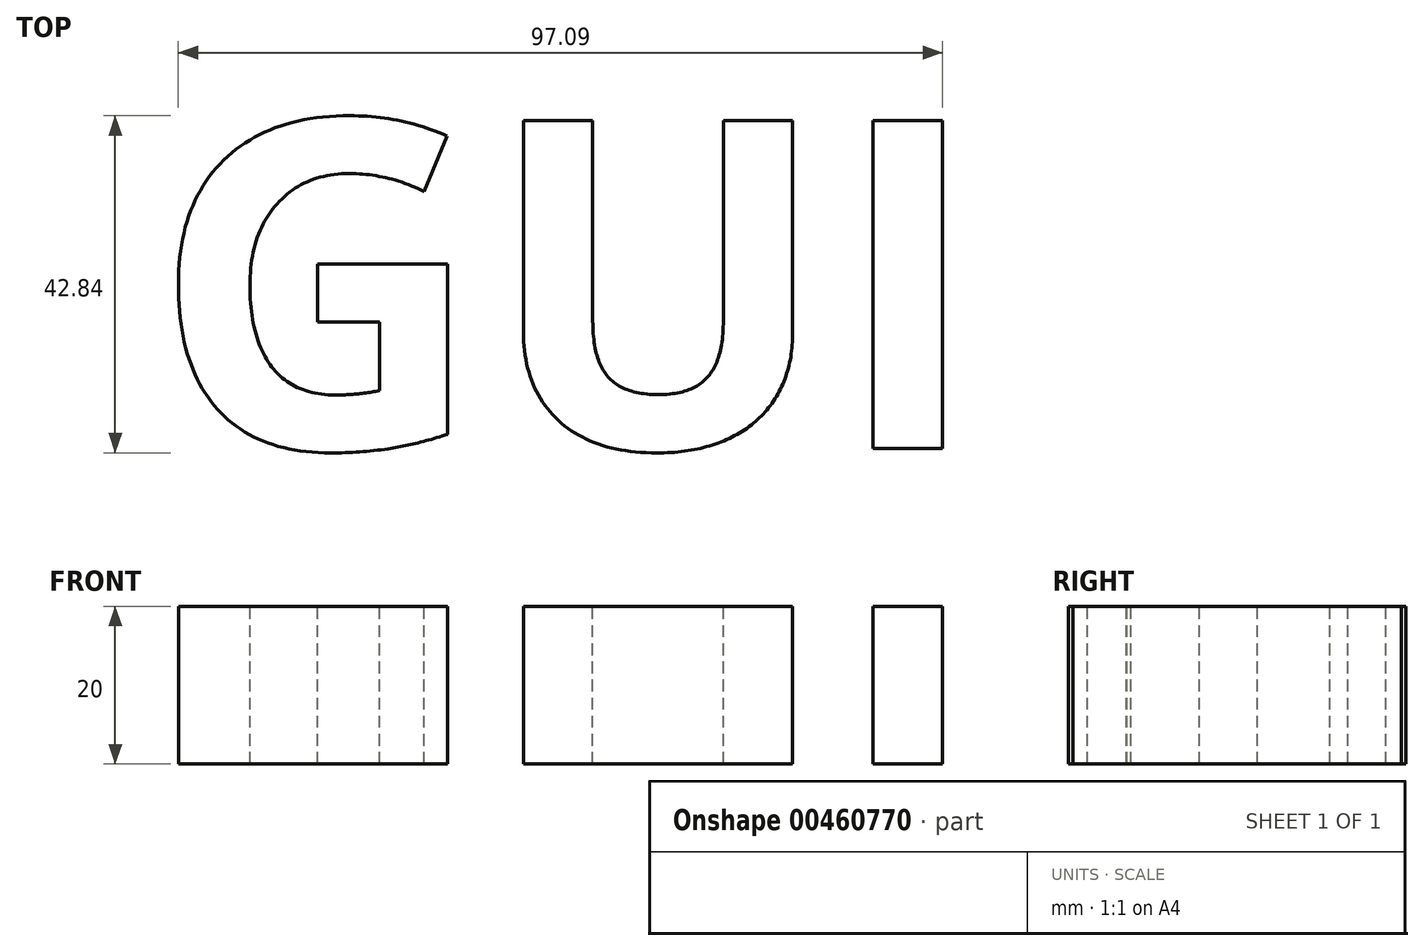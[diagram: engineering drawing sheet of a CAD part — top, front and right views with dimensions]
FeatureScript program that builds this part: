
annotation { "Feature Type Name" : "Feature", "Feature Type Description" : "" }
export const myFeature = defineFeature(function(context is Context, id is Id, definition is map)
    precondition{}
    {
        {
            var Q0;
            Q0=qCreatedBy(makeId("Top.planeOp"),FACE);
            var sketch = newSketch(context, id + "F0", { "sketchPlane" : qUnion([Q0])});
            skText(sketch, "E0", { "text": "GUI", "fontName": "OpenSans-Bold.ttf"});
            const initialGuessF0  = {"E0": [-0.02879, -0.02187, 1, 0, 0.04203]};
            skSetInitialGuess(sketch, initialGuessF0);
            skSolve(sketch);
        }
        {
            var Q0;
            Q0 = qConstructionFilter(qBodyType(qCreatedBy(id + "F0" ,EDGE), BodyType.WIRE), ConstructionObject.NO);
            extrude(context, id + "F1", {"bodyType" : ToolBodyType.SURFACE, "surfaceEntities" : qUnion([Q0]), "depth" : 20 * mm});
        }
    });
